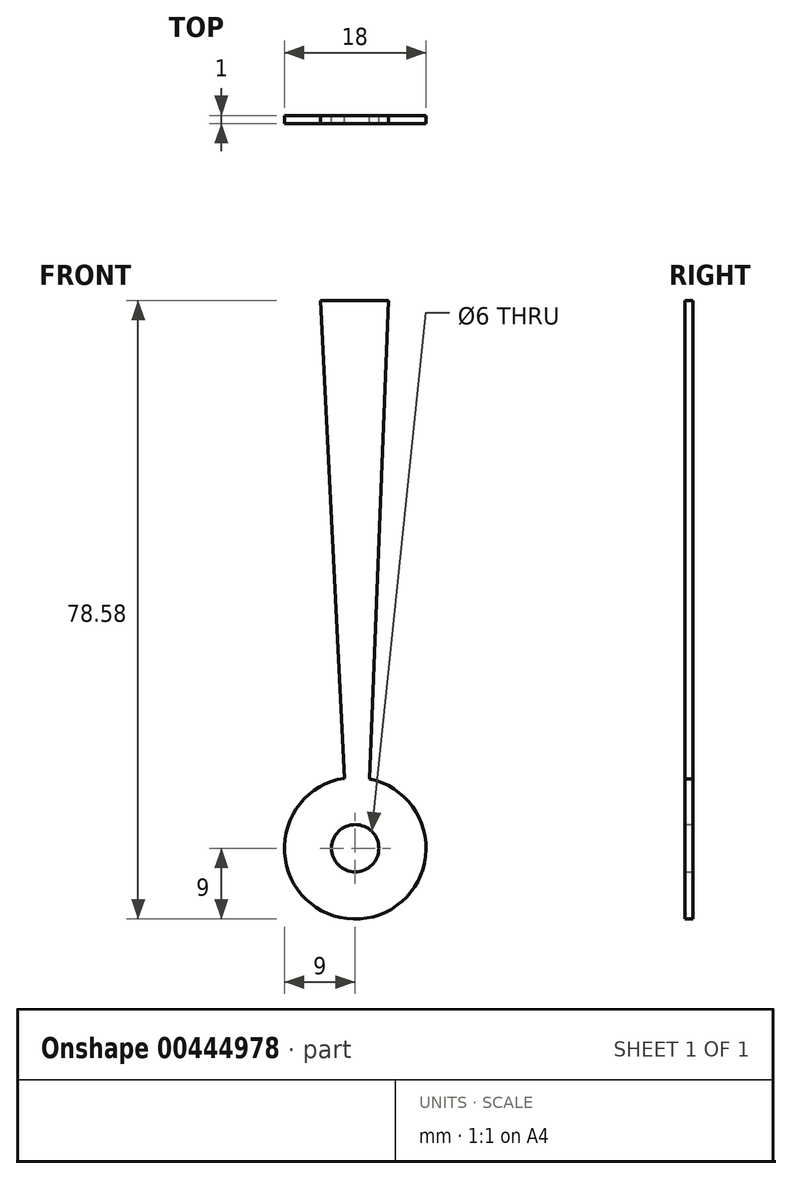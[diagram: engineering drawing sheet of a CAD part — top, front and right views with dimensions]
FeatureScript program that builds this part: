
annotation { "Feature Type Name" : "Feature", "Feature Type Description" : "" }
export const myFeature = defineFeature(function(context is Context, id is Id, definition is map)
    precondition{}
    {
        {
            var Q0;
            Q0=qCreatedBy(makeId("Front.planeOp"),FACE);
            var sketch = newSketch(context, id + "F0", { "sketchPlane" : qUnion([Q0])});
            skCircle(sketch, "E0", {"center": v(0, 0) * mm, "radius": 3 * mm});
            skCircle(sketch, "E1", {"center": v(0, 0) * mm, "radius": 9 * mm});
            skLineSegment(sketch, "E2", {"start": v(-4.4, 69.58) * mm, "end": v(4.2, 69.58) * mm});
            skLineSegment(sketch, "E3", {"start": v(4.2, 69.58) * mm, "end": v(1.8, 8.82) * mm});
            skLineSegment(sketch, "E4", {"start": v(-4.4, 69.58) * mm, "end": v(-1.37, 8.9) * mm});
            skSolve(sketch);
        }
        {
            var Q0;
            Q0 = qSketchRegion(id + "F0", true);
            extrude(context, id + "F1", {"entities" : qUnion([Q0]), "depth" : 1 * mm});
        }
    });
